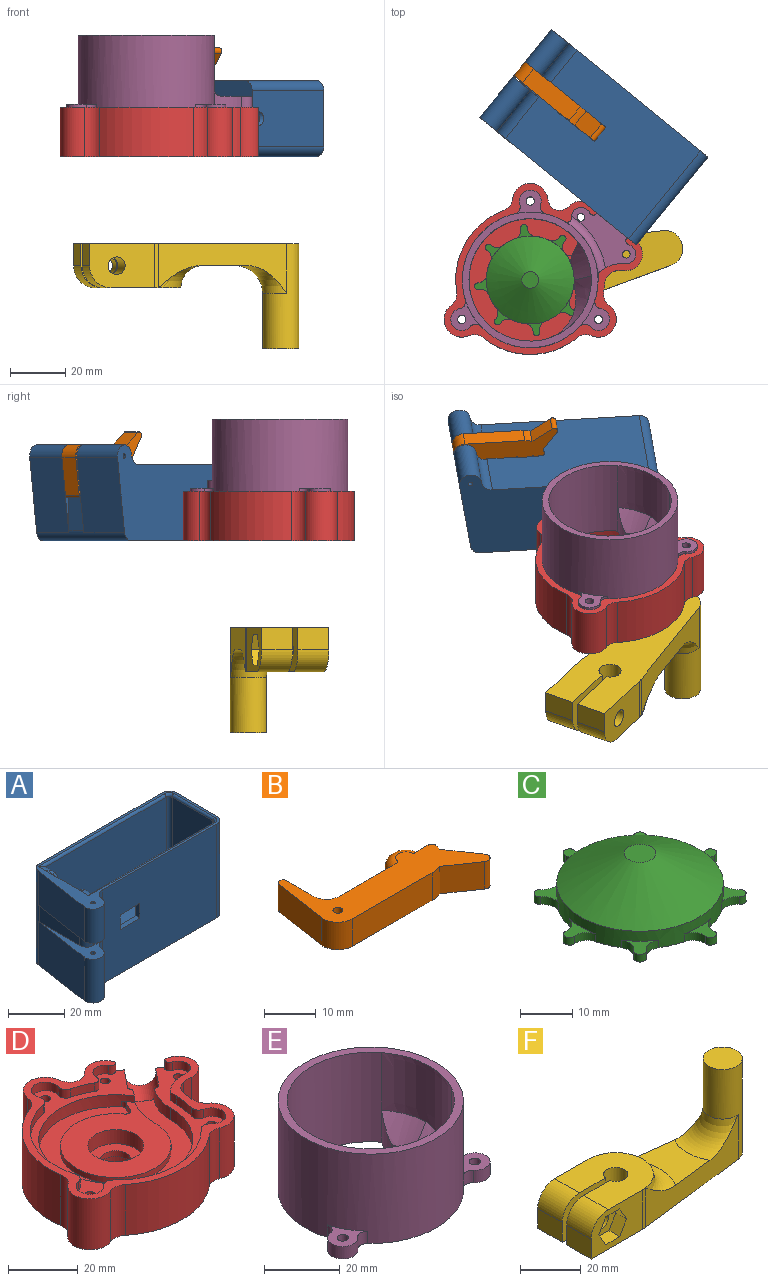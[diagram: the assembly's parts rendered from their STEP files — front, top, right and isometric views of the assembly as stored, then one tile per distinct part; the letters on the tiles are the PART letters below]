
ASSEMBLY  parts=6 mates=11
PART A: 56 faces, bbox 73x34.6x41 mm
  f0: plane 27.06x19mm, normal (-0.99,0.15,0), area 519.7mm2, adj f2,f6,f47,f55
  f1: cylinder r=4mm len=19mm, axis (0,0,-1), area 111.1mm2, adj f2,f5,f47,f55
  f2: cylinder r=4mm len=19mm, axis (0,0,-1), area 241.6mm2, adj f0,f1,f47,f55
  f3: cylinder r=0.79mm len=19mm, axis (0,0,-1), area 94.8mm2, adj f47,f55
  f4: cylinder r=0.79mm len=15mm, axis (0,0,-1), area 74.8mm2, adj f25,f54
  f5: plane 62x41mm, normal (0,-1,0), area 2325.6mm2, adj f1,f9,f10,f25,f31,f32,f33,f34
  f6: cylinder r=3.5mm len=41mm, axis (0,0,-1), area 208mm2, adj f0,f8,f13,f25,f47,f52,f54,f55
  f7: plane 60.95x29mm, normal (0,1,0), area 1668.8mm2, adj f21,f22,f26,f31,f32,f33,f34,f37
  f8: plane 20.5x7mm, normal (-1,0,0), area 143.5mm2, adj f6,f9,f54,f55
  f9: cylinder r=3.5mm len=7mm, axis (0,0,-1), area 38.5mm2, adj f5,f8,f54,f55
  f10: cylinder r=3.5mm len=41mm, axis (0,0,-1), area 225.4mm2, adj f5,f11,f25,f47
  f11: plane 41x20.5mm, normal (1,0,0), area 821.6mm2, adj f10,f12,f25,f47,f53
  f12: cylinder r=3.5mm len=41mm, axis (0,0,-1), area 225.4mm2, adj f11,f13,f25,f47
  f13: plane 62x41mm, normal (0,1,0), area 2542mm2, adj f6,f12,f25,f47
  f14: plane 30x19mm, normal (1,0,0), area 351mm2, adj f15,f24,f25,f26,f35,f38
  f15: plane 26.25x2.25mm, normal (0,-1,0), area 59.1mm2, adj f14,f16,f26,f38
  f16: cylinder r=1.5mm len=26.25mm, axis (0,0,-1), area 61.9mm2, adj f15,f17,f26,f39
  f17: plane 26.25x4.5mm, normal (1,0,0), area 118.1mm2, adj f16,f18,f26,f40
  f18: plane 60.95x29mm, normal (0,-1,0), area 1733.8mm2, adj f17,f19,f26,f40,f45
  f19: cylinder r=1.5mm len=29mm, axis (0,0,-1), area 68.3mm2, adj f18,f20,f26,f44
  f20: plane 29x20.5mm, normal (-1,0,0), area 594.5mm2, adj f19,f21,f26,f43
  f21: cylinder r=1.5mm len=29mm, axis (0,0,-1), area 68.3mm2, adj f7,f20,f26,f42
  f22: plane 26.25x4.5mm, normal (1,0,0), area 118.1mm2, adj f7,f23,f26,f37
  f23: cylinder r=1.5mm len=26.25mm, axis (0,0,-1), area 61.9mm2, adj f22,f24,f26,f36
  f24: plane 26.25x2.25mm, normal (0,1,0), area 59.1mm2, adj f14,f23,f26,f35
  f25: plane 73x34.63mm, normal (0,0,1), area 303.6mm2, adj f4,f5,f6,f10,f11,f12,f13,f14
  f26: plane 65x23.5mm, normal (0,0,1), area 934.4mm2, adj f7,f14,f15,f16,f17,f18,f19,f20
  f27: cylinder r=6.75mm len=13.5mm, axis (0,0,1), area 63.6mm2, adj f26,f28,f30,f46
  f28: plane 30x3mm, normal (0,-1,0), area 90mm2, adj f26,f27,f29,f46
  f29: cylinder r=6.75mm len=13.5mm, axis (0,0,1), area 63.6mm2, adj f26,f28,f30,f46
  f30: plane 30x3mm, normal (0,1,0), area 90mm2, adj f26,f27,f29,f46
  f31: plane 10x2mm, normal (0,0,1), area 20mm2, adj f5,f7,f32,f33
  f32: plane 6.5x2mm, normal (1,0,0), area 13mm2, adj f5,f7,f31,f34
  f33: plane 6.5x2mm, normal (-1,0,0), area 13mm2, adj f5,f7,f31,f34
  f34: plane 10x2mm, normal (0,0,-1), area 20mm2, adj f5,f7,f32,f33
  f35: cylinder r=3.75mm len=3.75mm, axis (1,0,0), area 8.4mm2, adj f14,f24,f36
  f36: bspline ~4.43x3.75mm, area 9.4mm2, adj f23,f35,f37
  f37: cylinder r=3.75mm len=5.5mm, axis (0,-1,0), area 22.8mm2, adj f7,f22,f25,f36,f41
  f38: cylinder r=3.75mm len=3.75mm, axis (-1,0,0), area 8.4mm2, adj f14,f15,f39
  f39: bspline ~4.43x3.75mm, area 9.4mm2, adj f16,f38,f40
  f40: cylinder r=3.75mm len=5.5mm, axis (0,-1,0), area 22.8mm2, adj f17,f18,f25,f39,f45
  f41: cylinder r=1mm len=63.5mm, axis (1,0,0), area 97.6mm2, adj f7,f25,f37,f42
  f42: torus R=2.5mm, axis (0,0,1), area 4.6mm2, adj f21,f25,f41,f43
  f43: cylinder r=1mm len=20.5mm, axis (0,1,0), area 32.2mm2, adj f20,f25,f42,f44
  f44: torus R=2.5mm, axis (0,0,1), area 4.6mm2, adj f19,f25,f43,f45
  f45: cylinder r=1mm len=63.5mm, axis (-1,0,0), area 97.6mm2, adj f18,f25,f40,f44
  f46: plane 43.5x13.5mm, normal (0,0,1), area 497.9mm2, adj f27,f28,f29,f30,f48
  f47: plane 73x34.63mm, normal (0,0,-1), area 1933.7mm2, adj f0,f1,f2,f3,f5,f6,f10,f11
  f48: cylinder r=4mm len=8mm, axis (0,0,1), area 194.3mm2, adj f46,f47,f49
  f49: cylinder r=1.45mm len=6.52mm, axis (1,0,0), area 58.2mm2, adj f48,f53
  f50: cylinder r=4mm len=15mm, axis (0,0,-1), area 87.7mm2, adj f5,f25,f51,f54
  f51: cylinder r=4mm len=15mm, axis (0,0,-1), area 190.8mm2, adj f25,f50,f52,f54
  f52: plane 27.06x15mm, normal (-0.99,0.15,0), area 410.3mm2, adj f6,f25,f51,f54
  f53: cone r=1.45mm half-angle=45deg, axis (1,0,0), area 17.3mm2, adj f11,f49
  f54: plane 31.64x11.95mm, normal (0,0,-1), area 96.9mm2, adj f4,f5,f6,f8,f9,f50,f51,f52
  f55: plane 31.64x11.95mm, normal (0,0,1), area 96.9mm2, adj f0,f1,f2,f3,f5,f6,f8,f9
PART B: 20 faces, bbox 37.6x23.8x6.5 mm
  f0: plane 37.63x23.77mm, normal (0,0,1), area 292.8mm2, adj f1,f2,f3,f4,f5,f6,f7,f8
  f1: plane 13.58x6.5mm, normal (-0.99,0.15,0), area 89.3mm2, adj f0,f2,f12,f17
  f2: cylinder r=4mm len=6.5mm, axis (0,0,-1), area 44.7mm2, adj f0,f1,f3,f12
  f3: plane 21.75x6.5mm, normal (0,-1,0), area 141.4mm2, adj f0,f2,f4,f12
  f4: cylinder r=7.13mm len=6.5mm, axis (0,0,-1), area 17.3mm2, adj f0,f3,f5,f12
  f5: plane 7.29x6.5mm, normal (-0.57,-0.82,0), area 57.5mm2, adj f0,f4,f6,f12
  f6: cylinder r=1.27mm len=6.5mm, axis (0,0,-1), area 22.9mm2, adj f0,f5,f7,f12
  f7: plane 7.29x6.5mm, normal (0.82,0.57,0), area 57.5mm2, adj f0,f6,f8,f12
  f8: cylinder r=7.13mm len=6.5mm, axis (0,0,-1), area 9.7mm2, adj f0,f7,f9,f12
  f9: cylinder r=1mm len=6.5mm, axis (0,0,-1), area 11.3mm2, adj f0,f8,f10,f12
  f10: plane 6.5x4.05mm, normal (0,1,0), area 15mm2, adj f0,f9,f11,f12,f18,f19
  f11: cylinder r=4mm len=8mm, axis (0,0,-1), area 31.4mm2, adj f10,f14,f18,f19
  f12: plane 37.63x23.77mm, normal (0,0,-1), area 292.8mm2, adj f1,f2,f3,f4,f5,f6,f7,f8
  f13: cylinder r=0.95mm len=6.5mm, axis (0,0,-1), area 38.9mm2, adj f0,f12
  f14: plane 16.25x6.5mm, normal (0,1,0), area 94.3mm2, adj f0,f11,f12,f16,f18,f19
  f15: plane 6.88x6.5mm, normal (1,0,0), area 44.7mm2, adj f0,f12,f16,f17
  f16: cylinder r=3.5mm len=6.5mm, axis (0,0,-1), area 39.1mm2, adj f0,f12,f14,f15
  f17: cylinder r=1mm len=6.5mm, axis (0,0,1), area 19.5mm2, adj f0,f1,f12,f15
  f18: torus R=2mm, axis (0,0,1), area 32.3mm2, adj f0,f10,f11,f14
  f19: torus R=2mm, axis (0,0,1), area 32.3mm2, adj f10,f11,f12,f14
PART C: 42 faces, bbox 40.5x40.5x11.1 mm
  f0: plane 40.46x40.46mm, normal (0,0,-1), area 843.4mm2, adj f9,f10,f11,f12,f13,f14,f15,f16
  f1: plane 6.55x5.5mm, normal (-1,0,0), area 36mm2, adj f38,f39,f41
  f2: plane 6.24x6.24mm, normal (0,0,1), area 12.4mm2, adj f9,f16,f17,f18
  f3: plane 7.18x4.74mm, normal (0,0,1), area 12.4mm2, adj f9,f19,f20,f21
  f4: plane 6.24x6.24mm, normal (0,0,1), area 12.4mm2, adj f9,f22,f23,f24
  f5: plane 7.18x4.74mm, normal (0,0,1), area 12.4mm2, adj f9,f25,f26,f27
  f6: plane 6.24x6.24mm, normal (0,0,1), area 12.4mm2, adj f9,f28,f29,f30
  f7: plane 7.18x4.74mm, normal (0,0,1), area 12.4mm2, adj f9,f31,f32,f33
  f8: plane 7.18x4.74mm, normal (0,0,1), area 12.4mm2, adj f13,f14,f15,f35
  f9: cylinder r=15.91mm len=31.81mm, axis (0,0,-1), area 291.1mm2, adj f0,f2,f3,f4,f5,f6,f7,f10
  f10: cylinder r=3.12mm len=4.1mm, axis (0,0,-1), area 8.2mm2, adj f0,f9,f11,f34
  f11: cylinder r=1.2mm len=2.14mm, axis (0,0,-1), area 7.3mm2, adj f0,f10,f12,f34
  f12: cylinder r=3.12mm len=4.1mm, axis (0,0,-1), area 8.2mm2, adj f0,f9,f11,f34
  f13: cylinder r=3.12mm len=3.4mm, axis (0,0,-1), area 8.2mm2, adj f0,f8,f9,f14
  f14: cylinder r=1.2mm len=2.4mm, axis (0,0,-1), area 7.3mm2, adj f0,f8,f13,f15
  f15: cylinder r=3.12mm len=3.4mm, axis (0,0,-1), area 8.2mm2, adj f0,f8,f9,f14
  f16: cylinder r=3.12mm len=4.1mm, axis (0,0,-1), area 8.2mm2, adj f0,f2,f9,f17
  f17: cylinder r=1.2mm len=2.14mm, axis (0,0,-1), area 7.3mm2, adj f0,f2,f16,f18
  f18: cylinder r=3.12mm len=4.1mm, axis (0,0,-1), area 8.2mm2, adj f0,f2,f9,f17
  f19: cylinder r=3.12mm len=3.4mm, axis (0,0,-1), area 8.2mm2, adj f0,f3,f9,f20
  f20: cylinder r=1.2mm len=2.4mm, axis (0,0,-1), area 7.3mm2, adj f0,f3,f19,f21
  f21: cylinder r=3.12mm len=3.4mm, axis (0,0,-1), area 8.2mm2, adj f0,f3,f9,f20
  f22: cylinder r=3.12mm len=4.1mm, axis (0,0,-1), area 8.2mm2, adj f0,f4,f9,f23
  f23: cylinder r=1.2mm len=2.14mm, axis (0,0,-1), area 7.3mm2, adj f0,f4,f22,f24
  f24: cylinder r=3.12mm len=4.1mm, axis (0,0,-1), area 8.2mm2, adj f0,f4,f9,f23
  f25: cylinder r=3.12mm len=3.4mm, axis (0,0,-1), area 8.2mm2, adj f0,f5,f9,f26
  f26: cylinder r=1.2mm len=2.4mm, axis (0,0,-1), area 7.3mm2, adj f0,f5,f25,f27
  f27: cylinder r=3.12mm len=3.4mm, axis (0,0,-1), area 8.2mm2, adj f0,f5,f9,f26
  f28: cylinder r=3.12mm len=4.1mm, axis (0,0,-1), area 8.2mm2, adj f0,f6,f9,f29
  f29: cylinder r=1.2mm len=2.14mm, axis (0,0,-1), area 7.3mm2, adj f0,f6,f28,f30
  f30: cylinder r=3.12mm len=4.1mm, axis (0,0,-1), area 8.2mm2, adj f0,f6,f9,f29
  f31: cylinder r=3.12mm len=3.4mm, axis (0,0,-1), area 8.2mm2, adj f0,f7,f9,f32
  f32: cylinder r=1.2mm len=2.4mm, axis (0,0,-1), area 7.3mm2, adj f0,f7,f31,f33
  f33: cylinder r=3.12mm len=3.4mm, axis (0,0,-1), area 8.2mm2, adj f0,f7,f9,f32
  f34: plane 6.24x6.24mm, normal (0,0,1), area 12.4mm2, adj f9,f10,f11,f12
  f35: extruded ~7.18x2.33mm, area 16.8mm2, adj f8,f9,f37
  f36: plane 6x6mm, normal (0,0,1), area 28.3mm2, adj f37
  f37: cone r=3mm half-angle=61.5deg, axis (0,0,-1), area 872.1mm2, adj f9,f35,f36
  f38: cylinder r=4mm len=8mm, axis (0,0,-1), area 139.7mm2, adj f0,f1,f39,f40
  f39: plane 8x6.3mm, normal (0,0,-1), area 42.5mm2, adj f1,f38
  f40: extruded ~6.55x2.5mm, area 19.2mm2, adj f0,f38,f41
  f41: plane 6.55x1.7mm, normal (0,0,-1), area 7.8mm2, adj f1,f40
PART D: 67 faces, bbox 71.8x61.9x17.9 mm
  f0: plane 0.79x0.02mm, normal (0.63,0.78,0), area 0mm2, adj f8,f63
  f1: plane 0.61x0.5mm, normal (0.63,0.78,0), area 0mm2, adj f9,f63
  f2: plane 66.96x57.11mm, normal (0,0,1), area 649.2mm2, adj f4,f8,f10,f11,f12,f13,f14,f15
  f3: cylinder r=4.5mm len=9mm, axis (0,0,-1), area 56.5mm2, adj f19,f20
  f4: cylinder r=22.16mm len=14.53mm, axis (0,0,1), area 38mm2, adj f2,f5,f9,f13,f18,f61,f63
  f5: cylinder r=15.91mm len=31.81mm, axis (0,0,1), area 179.9mm2, adj f4,f9,f18,f64
  f6: cylinder r=24.56mm len=3mm, axis (0,0,-1), area 6.7mm2, adj f9,f18,f64,f65
  f7: cylinder r=8mm len=16mm, axis (0,0,1), area 251.3mm2, adj f18,f19
  f8: cylinder r=15.91mm len=10.6mm, axis (0,0,1), area 46.7mm2, adj f0,f2,f9,f13,f63
  f9: plane 48.36x44.31mm, normal (0,0,1), area 758.6mm2, adj f1,f4,f5,f6,f8,f13,f63,f64
  f10: cylinder r=1.5mm len=14.88mm, axis (0,0,-1), area 140.2mm2, adj f2,f66
  f11: cylinder r=1.5mm len=14.88mm, axis (0,0,-1), area 140.2mm2, adj f2,f66
  f12: cylinder r=1.5mm len=14.88mm, axis (0,0,-1), area 140.2mm2, adj f2,f66
  f13: cylinder r=22.16mm len=44.31mm, axis (0,0,1), area 533.6mm2, adj f2,f4,f8,f9,f18,f65
  f14: plane 14.88x11.19mm, normal (0.63,0.78,0), area 170.4mm2, adj f2,f41,f49,f62,f66
  f15: cylinder r=1.4mm len=14.88mm, axis (0,0,-1), area 130.8mm2, adj f2,f66
  f16: cylinder r=1.4mm len=14.88mm, axis (0,0,-1), area 130.8mm2, adj f2,f66
  f17: cylinder r=8mm len=16mm, axis (0,0,-1), area 282.7mm2, adj f20,f66
  f18: plane 34.94x31.81mm, normal (0,0,1), area 616.8mm2, adj f4,f5,f6,f7,f13,f64,f65
  f19: plane 16x16mm, normal (0,0,1), area 137.4mm2, adj f3,f7
  f20: plane 16x16mm, normal (0,0,-1), area 137.4mm2, adj f3,f17
  f21: cylinder r=3.5mm len=6.87mm, axis (0,0,-1), area 31.2mm2, adj f2,f32,f33,f50
  f22: cylinder r=4mm len=7.94mm, axis (0,0,-1), area 46mm2, adj f2,f23,f36,f50
  f23: cylinder r=2.5mm len=3.74mm, axis (0,0,-1), area 12.7mm2, adj f2,f22,f24,f50
  f24: cylinder r=24.56mm len=35.88mm, axis (0,0,-1), area 120.7mm2, adj f2,f23,f25,f50
  f25: cylinder r=2.5mm len=3.74mm, axis (0,0,-1), area 12.7mm2, adj f2,f24,f26,f50
  f26: cylinder r=4mm len=7.94mm, axis (0,0,-1), area 46mm2, adj f2,f25,f27,f50
  f27: cylinder r=2.5mm len=3.19mm, axis (0,0,-1), area 12.7mm2, adj f2,f26,f28,f50
  f28: cylinder r=24.56mm len=31.07mm, axis (0,0,-1), area 120.7mm2, adj f2,f27,f29,f50
  f29: cylinder r=2.5mm len=3.28mm, axis (0,0,-1), area 12.7mm2, adj f2,f28,f30,f50
  f30: cylinder r=4mm len=8mm, axis (0,0,-1), area 46mm2, adj f2,f29,f37,f50
  f31: cylinder r=3.5mm len=6.61mm, axis (0,0,-1), area 28.7mm2, adj f2,f39,f40,f50
  f32: cylinder r=1.5mm len=3mm, axis (0,0,-1), area 8.5mm2, adj f2,f21,f50,f51
  f33: cylinder r=12mm len=9.57mm, axis (0,0,-1), area 31.3mm2, adj f2,f21,f34,f50
  f34: cylinder r=13.51mm len=3mm, axis (0,0,-1), area 7.7mm2, adj f2,f33,f35,f50
  f35: cylinder r=24.56mm len=7.15mm, axis (0,0,-1), area 21.8mm2, adj f2,f34,f36,f50
  f36: cylinder r=2.5mm len=3.19mm, axis (0,0,-1), area 12.7mm2, adj f2,f22,f35,f50
  f37: cylinder r=2.5mm len=3.28mm, axis (0,0,-1), area 12.7mm2, adj f2,f30,f38,f50
  f38: cylinder r=24.56mm len=7.07mm, axis (0,0,-1), area 23mm2, adj f2,f37,f39,f50
  f39: cylinder r=1.5mm len=3mm, axis (0,0,-1), area 9.8mm2, adj f2,f31,f38,f50
  f40: cylinder r=1.5mm len=3mm, axis (0,0,-1), area 8.5mm2, adj f2,f31,f50,f52
  f41: cylinder r=5.9mm len=17.88mm, axis (0,0,-1), area 220.9mm2, adj f14,f50,f52,f54,f66
  f42: cylinder r=6.4mm len=17.88mm, axis (0,0,-1), area 332.7mm2, adj f50,f53,f55,f66
  f43: cylinder r=26.96mm len=29.54mm, axis (0,0,-1), area 660.1mm2, adj f50,f55,f56,f66
  f44: cylinder r=6.4mm len=17.88mm, axis (0,0,-1), area 332.7mm2, adj f50,f56,f57,f66
  f45: cylinder r=26.96mm len=34.11mm, axis (0,0,-1), area 660.1mm2, adj f50,f57,f58,f66
  f46: cylinder r=6.4mm len=17.88mm, axis (0,0,-1), area 332.7mm2, adj f50,f58,f59,f66
  f47: cylinder r=26.96mm len=17.88mm, axis (0,0,-1), area 53mm2, adj f50,f59,f60,f66
  f48: cylinder r=9.6mm len=17.88mm, axis (0,0,-1), area 63.7mm2, adj f49,f50,f60,f66
  f49: cylinder r=5.9mm len=17.88mm, axis (0,0,-1), area 333.4mm2, adj f14,f48,f50,f51,f66
  f50: plane 71.76x61.91mm, normal (0,0,1), area 532.4mm2, adj f21,f22,f23,f24,f25,f26,f27,f28
  f51: cylinder r=0.5mm len=3mm, axis (0,0,1), area 1.4mm2, adj f2,f32,f49,f50
  f52: cylinder r=0.5mm len=3mm, axis (0,0,1), area 1.4mm2, adj f2,f40,f41,f50
  f53: cylinder r=5mm len=17.88mm, axis (0,0,1), area 90.9mm2, adj f42,f50,f54,f66
  f54: cylinder r=5mm len=17.88mm, axis (0,0,1), area 95.5mm2, adj f41,f50,f53,f66
  f55: cylinder r=5mm len=17.88mm, axis (0,0,1), area 97.6mm2, adj f42,f43,f50,f66
  f56: cylinder r=5mm len=17.88mm, axis (0,0,1), area 97.6mm2, adj f43,f44,f50,f66
  f57: cylinder r=5mm len=17.88mm, axis (0,0,1), area 97.6mm2, adj f44,f45,f50,f66
  f58: cylinder r=5mm len=17.88mm, axis (0,0,1), area 97.6mm2, adj f45,f46,f50,f66
  f59: cylinder r=5mm len=17.88mm, axis (0,0,1), area 97.6mm2, adj f46,f47,f50,f66
  f60: cylinder r=5mm len=17.88mm, axis (0,0,-1), area 111.9mm2, adj f47,f48,f50,f66
  f61: plane 0.79x0.02mm, normal (0.63,0.78,0), area 0mm2, adj f4,f63
  f62: cylinder r=4.65mm len=12.58mm, axis (0.63,0.78,0), area 143.5mm2, adj f2,f14,f63
  f63: torus R=3.15mm, axis (0.63,0.78,0), area 31.4mm2, adj f0,f1,f2,f4,f8,f9,f61,f62
  f64: cylinder r=1.5mm len=2.59mm, axis (0,0,1), area 6.3mm2, adj f5,f6,f9,f18
  f65: cylinder r=1.5mm len=2mm, axis (0,0,-1), area 3.7mm2, adj f6,f9,f13,f18
  f66: plane 71.76x61.91mm, normal (0,0,-1), area 2645.4mm2, adj f10,f11,f12,f14,f15,f16,f17,f41
PART E: 48 faces, bbox 67.7x62x30.4 mm
  f0: cylinder r=22.16mm len=44.31mm, axis (0,0,-1), area 3257mm2, adj f28,f30,f31,f33,f36,f37,f43,f44
  f1: plane 11.19x9.12mm, normal (0.63,0.78,0), area 77.4mm2, adj f10,f11,f30,f38,f39
  f2: cylinder r=24.56mm len=49.11mm, axis (0,0,-1), area 4086.9mm2, adj f3,f4,f6,f14,f15,f17,f18,f20
  f3: plane 11.1x8.64mm, normal (0,0,1), area 50.2mm2, adj f2,f15,f16,f17,f27
  f4: plane 11.13x10.79mm, normal (0,0,1), area 50.2mm2, adj f2,f18,f19,f20,f26
  f5: cylinder r=22.16mm len=10.73mm, axis (0,0,-1), area 23.4mm2, adj f30,f31,f41,f42
  f6: cylinder r=13.51mm len=10mm, axis (0,0,-1), area 23.9mm2, adj f2,f7,f30,f47
  f7: cylinder r=12mm len=9.57mm, axis (0,0,-1), area 75.5mm2, adj f6,f8,f30,f38,f47
  f8: cylinder r=3.5mm len=7mm, axis (0,0,-1), area 72.8mm2, adj f7,f9,f30,f38
  f9: cylinder r=1.5mm len=7mm, axis (0,0,-1), area 19.9mm2, adj f8,f10,f30,f38
  f10: cylinder r=0.5mm len=7mm, axis (0,0,-1), area 3.2mm2, adj f1,f9,f30,f38
  f11: cylinder r=0.5mm len=7mm, axis (0,0,-1), area 3.2mm2, adj f1,f12,f30,f38
  f12: cylinder r=1.5mm len=7mm, axis (0,0,-1), area 19.9mm2, adj f11,f13,f30,f38
  f13: cylinder r=3.5mm len=7.07mm, axis (0,0,-1), area 66.9mm2, adj f12,f14,f30,f38,f47
  f14: cylinder r=1.5mm len=10mm, axis (0,0,-1), area 27.8mm2, adj f2,f13,f30,f47
  f15: cylinder r=2.5mm len=4mm, axis (0,0,-1), area 16.9mm2, adj f2,f3,f16,f30
  f16: cylinder r=4mm len=8mm, axis (0,0,-1), area 61.3mm2, adj f3,f15,f17,f30
  f17: cylinder r=2.5mm len=4mm, axis (0,0,-1), area 16.9mm2, adj f2,f3,f16,f30
  f18: cylinder r=2.5mm len=4mm, axis (0,0,-1), area 16.9mm2, adj f2,f4,f19,f30
  f19: cylinder r=4mm len=7.94mm, axis (0,0,-1), area 61.3mm2, adj f4,f18,f20,f30
  f20: cylinder r=2.5mm len=4mm, axis (0,0,-1), area 16.9mm2, adj f2,f4,f19,f30
  f21: cylinder r=2.5mm len=4mm, axis (0,0,-1), area 16.9mm2, adj f2,f22,f30,f35
  f22: cylinder r=4mm len=7.94mm, axis (0,0,-1), area 61.3mm2, adj f21,f23,f30,f35
  f23: cylinder r=2.5mm len=4mm, axis (0,0,-1), area 16.9mm2, adj f2,f22,f30,f35
  f24: cylinder r=1.4mm len=7mm, axis (0,0,-1), area 61.6mm2, adj f30,f38
  f25: cylinder r=1.5mm len=4mm, axis (0,0,-1), area 37.7mm2, adj f30,f35
  f26: cylinder r=1.5mm len=4mm, axis (0,0,-1), area 37.7mm2, adj f4,f30
  f27: cylinder r=1.5mm len=4mm, axis (0,0,-1), area 37.7mm2, adj f3,f30
  f28: cylinder r=15.91mm len=10.6mm, axis (0,0,-1), area 22.5mm2, adj f0,f30,f31,f41
  f29: cylinder r=1.4mm len=7mm, axis (0,0,-1), area 61.6mm2, adj f30,f38
  f30: plane 67.2x57.35mm, normal (0,0,-1), area 669.2mm2, adj f0,f1,f2,f5,f6,f7,f8,f9
  f31: plane 33.38x14.16mm, normal (0,0,-1), area 138.4mm2, adj f0,f5,f28,f32,f34,f40,f41,f42
  f32: cylinder r=22.16mm len=4.17mm, axis (0,0,-1), area 4.3mm2, adj f31,f34,f43,f44,f45
  f33: cylinder r=24.56mm len=10.4mm, axis (0,0,-1), area 54.8mm2, adj f0,f30,f34,f46
  f34: cylinder r=15.91mm len=6.68mm, axis (0,0,-1), area 21mm2, adj f30,f31,f32,f33,f42,f46
  f35: plane 11.13x10.79mm, normal (0,0,1), area 50.2mm2, adj f2,f21,f22,f23,f25
  f36: extruded ~24.86x22.8mm, area 519.9mm2, adj f0,f37,f45,f46
  f37: plane 49.11x49.11mm, normal (0,0,1), area 352.2mm2, adj f0,f2,f36
  f38: plane 23.32x21.81mm, normal (0,0,1), area 202mm2, adj f1,f7,f8,f9,f10,f11,f12,f13
  f39: cylinder r=4.65mm len=12.37mm, axis (0.63,0.78,0), area 104.9mm2, adj f1,f30,f41
  f40: plane 0.61x0.5mm, normal (0.63,0.78,0), area 0mm2, adj f31,f41
  f41: torus R=3.15mm, axis (-0.63,-0.78,0), area 19.1mm2, adj f5,f28,f30,f31,f39,f40
  f42: cylinder r=0.4mm len=2mm, axis (0,0,-1), area 2.2mm2, adj f5,f30,f31,f34
  f43: cylinder r=15mm len=17.45mm, axis (0,0,-1), area 9.2mm2, adj f0,f32,f44,f45
  f44: cone r=15.8mm half-angle=45deg, axis (0,0,-1), area 23.9mm2, adj f0,f31,f32,f43
  f45: cone r=15.8mm half-angle=45deg, axis (0,0,1), area 122.1mm2, adj f0,f32,f36,f43,f46
  f46: bspline ~16.25x9.74mm, area 86.8mm2, adj f33,f34,f36,f45
  f47: torus R=27.56mm, axis (0,0,1), area 106.8mm2, adj f2,f6,f7,f13,f14,f38
PART F: 29 faces, bbox 80.5x56.3x38 mm
  f0: cylinder r=3.17mm len=6.5mm, axis (0,-1,0), area 129.7mm2, adj f8,f26
  f1: cylinder r=12.5mm len=16mm, axis (0,0,-1), area 24.1mm2, adj f3,f4,f14,f17
  f2: plane 20.92x18.09mm, normal (0,0,1), area 273.4mm2, adj f3,f12,f16,f18
  f3: plane 49.28x18mm, normal (0.12,0.99,0), area 493.7mm2, adj f1,f2,f13,f14,f16,f18
  f4: plane 24x16mm, normal (0,1,0), area 338.6mm2, adj f1,f5,f14,f17,f19,f28
  f5: plane 11.5x8mm, normal (-1,0,0), area 92mm2, adj f4,f6,f14,f28
  f6: plane 20.13x16mm, normal (0,-1,0), area 276.6mm2, adj f5,f7,f14,f17,f19,f28
  f7: cylinder r=4mm len=16mm, axis (0,0,-1), area 369.8mm2, adj f6,f8,f14,f17
  f8: plane 20.13x16mm, normal (0,1,0), area 276.6mm2, adj f0,f7,f9,f14,f17,f27
  f9: plane 11.5x8mm, normal (-1,0,0), area 92mm2, adj f8,f10,f14,f27
  f10: plane 24x16mm, normal (0,-1,0), area 260.7mm2, adj f9,f11,f14,f17,f20,f21,f22,f23
  f11: cylinder r=12.5mm len=16mm, axis (0,0,-1), area 24.1mm2, adj f10,f12,f14,f17
  f12: plane 49.28x18mm, normal (0.12,-0.99,0), area 493.7mm2, adj f2,f11,f13,f14,f16,f18
  f13: cylinder r=6.5mm len=38mm, axis (0,0,-1), area 1156.2mm2, adj f3,f12,f14,f15,f16
  f14: plane 80.5x25mm, normal (0,0,-1), area 1532.9mm2, adj f1,f3,f4,f5,f6,f7,f8,f9
  f15: plane 13x13mm, normal (0,0,1), area 132.7mm2, adj f13
  f16: torus R=16.5mm, axis (0,0,1), area 275.8mm2, adj f2,f3,f12,f13
  f17: plane 28.5x25mm, normal (0,0,1), area 571.1mm2, adj f1,f4,f6,f7,f8,f10,f11,f18
  f18: torus R=20.5mm, axis (0,0,1), area 340.6mm2, adj f2,f3,f12,f17
  f19: cylinder r=3.17mm len=11.5mm, axis (0,-1,0), area 229.4mm2, adj f4,f6
  f20: plane 5.63x5mm, normal (-0.87,0,-0.5), area 32.5mm2, adj f10,f21,f25,f26
  f21: plane 6.5x5mm, normal (0,0,-1), area 32.5mm2, adj f10,f20,f22,f26
  f22: plane 5.63x5mm, normal (0.87,0,-0.5), area 32.5mm2, adj f10,f21,f23,f26
  f23: plane 5.63x5mm, normal (0.87,0,0.5), area 32.5mm2, adj f10,f22,f24,f26
  f24: plane 6.5x5mm, normal (0,0,1), area 32.5mm2, adj f10,f23,f25,f26
  f25: plane 5.63x5mm, normal (-0.87,0,0.5), area 32.5mm2, adj f10,f20,f24,f26
  f26: plane 12.99x11.25mm, normal (0,-1,0), area 77.9mm2, adj f0,f20,f21,f22,f23,f24,f25
  f27: cylinder r=8mm len=11.5mm, axis (0,1,0), area 144.5mm2, adj f8,f9,f10,f17
  f28: cylinder r=8mm len=11.5mm, axis (0,1,0), area 144.5mm2, adj f4,f5,f6,f17
PLACE A rot(axis=(-0.89,0.32,-0.32),96.5deg) t=(16.67,40.67,9)mm
PLACE B rot(axis=(-0.89,0.32,-0.32),96.5deg) t=(16.83,40.86,9)mm
PLACE C rot(axis=(0,0,-1),38.1deg) t=(0,0,67.87)mm
PLACE D t=(0,0,-3)mm fixed
PLACE E t=(0,0,-3)mm
PLACE F rot(axis=(0.99,0.12,0),180deg) t=(0,0,-36.2)mm
MATE cylindrical E.f0 <-> D.f43  axis (0,0,-1) through (0,0,24.63)mm
MATE cylindrical A.f48 <-> D.f62  axis (0.63,0.78,0) through (32.16,22.88,9)mm
MATE planar B.f0 <-> A.f2  axis (0.63,0.78,0) through (9.74,69.55,29.88)mm
MATE planar E.f0 <-> D.f28  axis (0,0,-1) through (0,0,10.13)mm
MATE cylindrical E.f16 <-> D.f10  axis (0,0,-1) through (0,28.56,12.13)mm
MATE cylindrical C.f38 <-> D.f3  axis (0,0,-1) through (0,0,11.87)mm
MATE planar B.f14 <-> A.f5  axis (0,0,-1) through (7.59,67.1,22.75)mm
MATE cylindrical F.f7 <-> D.f3  axis (0,0,1) through (0,0,-44.2)mm
MATE planar C.f9 <-> D.f18  axis (0,0,-1) through (0,0,7.88)mm
MATE cylindrical B.f2 <-> A.f2  axis (-0.63,-0.78,0) through (-0.75,73.9,25.88)mm
MATE planar A.f47 <-> D.f14  axis (-0.63,-0.78,0) through (9.79,35.96,9.59)mm
